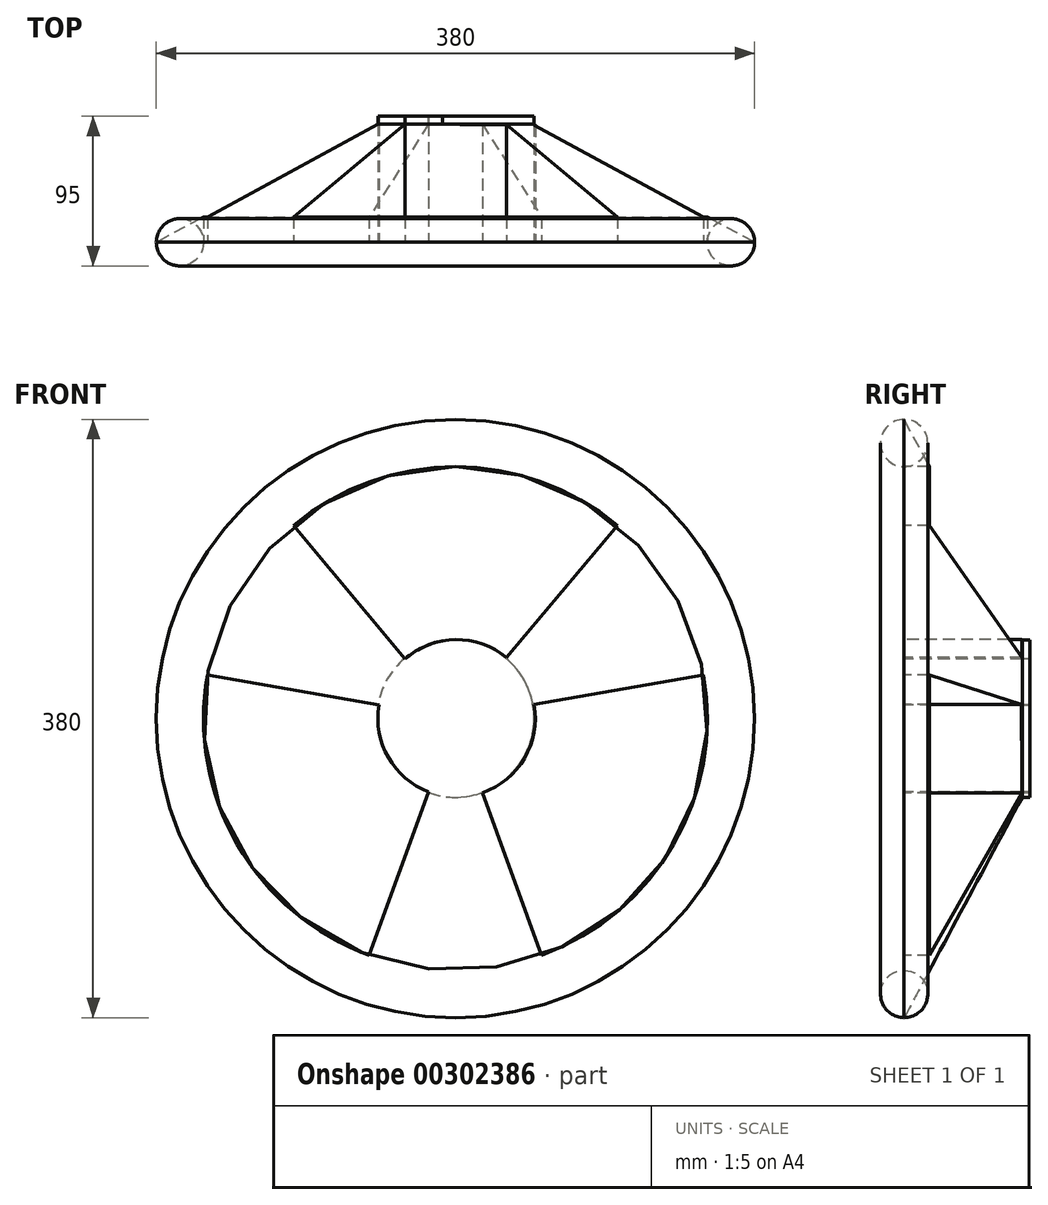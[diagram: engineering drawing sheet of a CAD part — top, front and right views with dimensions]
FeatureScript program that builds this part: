
annotation { "Feature Type Name" : "Feature", "Feature Type Description" : "" }
export const myFeature = defineFeature(function(context is Context, id is Id, definition is map)
    precondition{}
    {
        {
            var Q0;
            Q0=qCreatedBy(makeId("Right.planeOp"),FACE);
            var sketch = newSketch(context, id + "F0", { "sketchPlane" : qUnion([Q0])});
            skCircle(sketch, "E0", {"center": v(0, 175) * mm, "radius": 15 * mm});
            skLineSegment(sketch, "E1", {"start": v(0, 0) * mm, "end": v(-75.5, 0) * mm});
            skSolve(sketch);
        }
        {
            var Q0;
            Q0=makeQuery(id+"F0.imprint","IMPRINT",FACE,{"disambiguationData":[TD([[makeQuery(id+"F0.imprint","IMPRINT",EDGE,{"derivedFrom":sQuery(id+"F0.wireOp",EDGE,"E0")}),1.0]])]});
            var Q1;
            Q1=sQuery(id+"F0.wireOp",EDGE,"E1");
            revolve(context, id + "F1", {"entities" : qUnion([Q0]), "axis" : qUnion([Q1]), "revolveType" : RevolveType.FULL});
        }
        {
            var Q0;
            Q0=qCreatedBy(makeId("Front.planeOp"),FACE);
            cPlane(context, id + "F2", {"entities" : qUnion([Q0]), "cplaneType" : CPlaneType.OFFSET, "offset" : 80 * mm, "oppositeDirection" : true, "width" : 150 * mm, "height" : 150 * mm});
        }
        {
            var Q0;
            Q0=qCreatedBy(id+"F2.planeOp",FACE);
            var sketch = newSketch(context, id + "F3", { "sketchPlane" : qUnion([Q0])});
            skCircle(sketch, "E2", {"center": v(0, 0) * mm, "radius": 50 * mm});
            skSolve(sketch);
        }
        {
            var Q0;
            Q0 = qSketchRegion(id + "F3", true);
            extrude(context, id + "F4", {"entities" : qUnion([Q0]), "depth" : 5 * mm});
        }
        {
            var Q0;
            Q0=qCreatedBy(makeId("Top.planeOp"),FACE);
            var sketch = newSketch(context, id + "F5", { "sketchPlane" : qUnion([Q0])});
            skLineSegment(sketch, "E3", {"start": v(0, 0) * mm, "end": v(0, 75) * mm});
            skLineSegment(sketch, "E4", {"start": v(0, 75) * mm, "end": v(-50, 75) * mm});
            skLineSegment(sketch, "E5", {"start": v(-50, 75) * mm, "end": v(-190, 0) * mm});
            skLineSegment(sketch, "E6", {"start": v(-190, 0) * mm, "end": v(0, 0) * mm});
            skSolve(sketch);
        }
        {
            var Q0;
            Q0 = qSketchRegion(id + "F5", true);
            var Q1;
            Q1=sQuery(id+"F5.wireOp",EDGE,"E3");
            revolve(context, id + "F6", {"entities" : qUnion([Q0]), "axis" : qUnion([Q1]), "revolveType" : RevolveType.FULL});
        }
        {
            var Q0;
            Q0=makeQuery(id+"F6.opRevolve","SWEPT_FACE",FACE,{"disambiguationData":[OSD([sQuery(id+"F5.wireOp",EDGE,"E6")])]});
            var sketch = newSketch(context, id + "F7", { "sketchPlane" : qUnion([Q0])});
            skLineSegment(sketch, "E7", {"start": v(0, 0) * mm, "end": v(0, 160) * mm});
            skCircle(sketch, "E8.cCircle", {"center": v(0, 0) * mm, "radius": 160 * mm, "construction": true});
            skLineSegment(sketch, "E8.0", {"start": v(0, 160) * mm, "end": v(102.85, 122.57) * mm});
            skLineSegment(sketch, "E8.1", {"start": v(102.85, 122.57) * mm, "end": v(157.57, 27.78) * mm});
            skLineSegment(sketch, "E8.2", {"start": v(157.57, 27.78) * mm, "end": v(138.56, -80) * mm});
            skLineSegment(sketch, "E8.3", {"start": v(138.56, -80) * mm, "end": v(54.72, -150.35) * mm});
            skLineSegment(sketch, "E8.4", {"start": v(54.72, -150.35) * mm, "end": v(-54.72, -150.35) * mm});
            skLineSegment(sketch, "E8.5", {"start": v(-54.72, -150.35) * mm, "end": v(-138.56, -80) * mm});
            skLineSegment(sketch, "E8.6", {"start": v(-138.56, -80) * mm, "end": v(-157.57, 27.78) * mm});
            skLineSegment(sketch, "E8.7", {"start": v(-157.57, 27.78) * mm, "end": v(-102.85, 122.57) * mm});
            skLineSegment(sketch, "E8.8", {"start": v(-102.85, 122.57) * mm, "end": v(0, 160) * mm});
            skLineSegment(sketch, "E9", {"start": v(-157.57, 27.78) * mm, "end": v(0, 0) * mm});
            skLineSegment(sketch, "E10", {"start": v(-102.85, 122.57) * mm, "end": v(0, 0) * mm});
            skLineSegment(sketch, "E11", {"start": v(0, 0) * mm, "end": v(102.85, 122.57) * mm});
            skLineSegment(sketch, "E12", {"start": v(0, 0) * mm, "end": v(157.57, 27.78) * mm});
            skLineSegment(sketch, "E13", {"start": v(0, 0) * mm, "end": v(-54.72, -150.35) * mm});
            skLineSegment(sketch, "E14", {"start": v(0, 0) * mm, "end": v(54.72, -150.35) * mm});
            skArc(sketch, "E15", {"start": v(-157.57, 27.78) * mm, "mid": v(-157.52, -27.78) * mm, "end": v(-138.56, -80) * mm});
            skCircle(sketch, "E16", {"center": v(0, 0) * mm, "radius": 160 * mm});
            skLineSegment(sketch, "E17", {"start": v(-138.56, -80) * mm, "end": v(0.77, 0.14) * mm});
            skLineSegment(sketch, "E18", {"start": v(0.77, 0.14) * mm, "end": v(138.56, -80) * mm});
            skCircle(sketch, "E19", {"center": v(0.77, 0.14) * mm, "radius": 50 * mm});
            skSolve(sketch);
        }
        {
            var Q0;
            {var subQ0=sQuery(id+"F7.wireOp",EDGE,"E8.6");Q0=makeQuery(id+"F7.imprint","IMPRINT",FACE,{"disambiguationData":[TD([[makeQuery(id+"F7.imprint","IMPRINT",EDGE,{"derivedFrom":subQ0}),-1.0]])]});}
            var Q1;
            {var subQ1=sQuery(id+"F7.wireOp",EDGE,"E8.8");Q1=makeQuery(id+"F7.imprint","IMPRINT",FACE,{"disambiguationData":[TD([[makeQuery(id+"F7.imprint","IMPRINT",EDGE,{"derivedFrom":subQ1}),-1.0]])]});}
            var Q2;
            {var subQ1=sQuery(id+"F7.wireOp",EDGE,"E8.0");Q2=makeQuery(id+"F7.imprint","IMPRINT",FACE,{"disambiguationData":[TD([[makeQuery(id+"F7.imprint","IMPRINT",EDGE,{"derivedFrom":subQ1}),-1.0]])]});}
            var Q3;
            {var subQ0=sQuery(id+"F7.wireOp",EDGE,"E8.2");Q3=makeQuery(id+"F7.imprint","IMPRINT",FACE,{"disambiguationData":[TD([[makeQuery(id+"F7.imprint","IMPRINT",EDGE,{"derivedFrom":subQ0}),-1.0]])]});}
            var Q4;
            {var subQ0=sQuery(id+"F7.wireOp",EDGE,"E8.3");Q4=makeQuery(id+"F7.imprint","IMPRINT",FACE,{"disambiguationData":[TD([[makeQuery(id+"F7.imprint","IMPRINT",EDGE,{"derivedFrom":subQ0}),-1.0]])]});}
            var Q5;
            {var subQ0=sQuery(id+"F7.wireOp",EDGE,"E8.5");Q5=makeQuery(id+"F7.imprint","IMPRINT",FACE,{"disambiguationData":[TD([[makeQuery(id+"F7.imprint","IMPRINT",EDGE,{"derivedFrom":subQ0}),-1.0]])]});}
            var Q6;
            {var subQ0=sQuery(id+"F7.wireOp",EDGE,"E8.8");Q6=makeQuery(id+"F7.imprint","IMPRINT",FACE,{"disambiguationData":[TD([[makeQuery(id+"F7.imprint","IMPRINT",EDGE,{"derivedFrom":subQ0}),1.0]])]});}
            var Q7;
            {var subQ0=sQuery(id+"F7.wireOp",EDGE,"E8.0");Q7=makeQuery(id+"F7.imprint","IMPRINT",FACE,{"disambiguationData":[TD([[makeQuery(id+"F7.imprint","IMPRINT",EDGE,{"derivedFrom":subQ0}),1.0]])]});}
            var Q8;
            {var subQ0=sQuery(id+"F7.wireOp",EDGE,"E8.2");Q8=makeQuery(id+"F7.imprint","IMPRINT",FACE,{"disambiguationData":[TD([[makeQuery(id+"F7.imprint","IMPRINT",EDGE,{"derivedFrom":subQ0}),1.0]])]});}
            var Q9;
            {var subQ0=sQuery(id+"F7.wireOp",EDGE,"E8.3");Q9=makeQuery(id+"F7.imprint","IMPRINT",FACE,{"disambiguationData":[TD([[makeQuery(id+"F7.imprint","IMPRINT",EDGE,{"derivedFrom":subQ0}),1.0]])]});}
            var Q10;
            {var subQ0=sQuery(id+"F7.wireOp",EDGE,"E8.5");Q10=makeQuery(id+"F7.imprint","IMPRINT",FACE,{"disambiguationData":[TD([[makeQuery(id+"F7.imprint","IMPRINT",EDGE,{"derivedFrom":subQ0}),1.0]])]});}
            var Q11;
            Q11=makeQuery(id+"F7.imprint","IMPRINT",FACE,{"disambiguationData":[TD([[makeQuery(id+"F7.imprint","IMPRINT",EDGE,{"derivedFrom":sQuery(id+"F7.wireOp",EDGE,"E8.6")}),1.0]])]});
            extrude(context, id + "F8", {"entities" : qUnion([Q0, Q1, Q2, Q3, Q4, Q5, Q6, Q7, Q8, Q9, Q10, Q11]), "operationType" : NewBodyOperationType.REMOVE, "endBound" : BoundingType.THROUGH_ALL, "oppositeDirection" : true, "depth" : 25 * mm});
        }
    });
